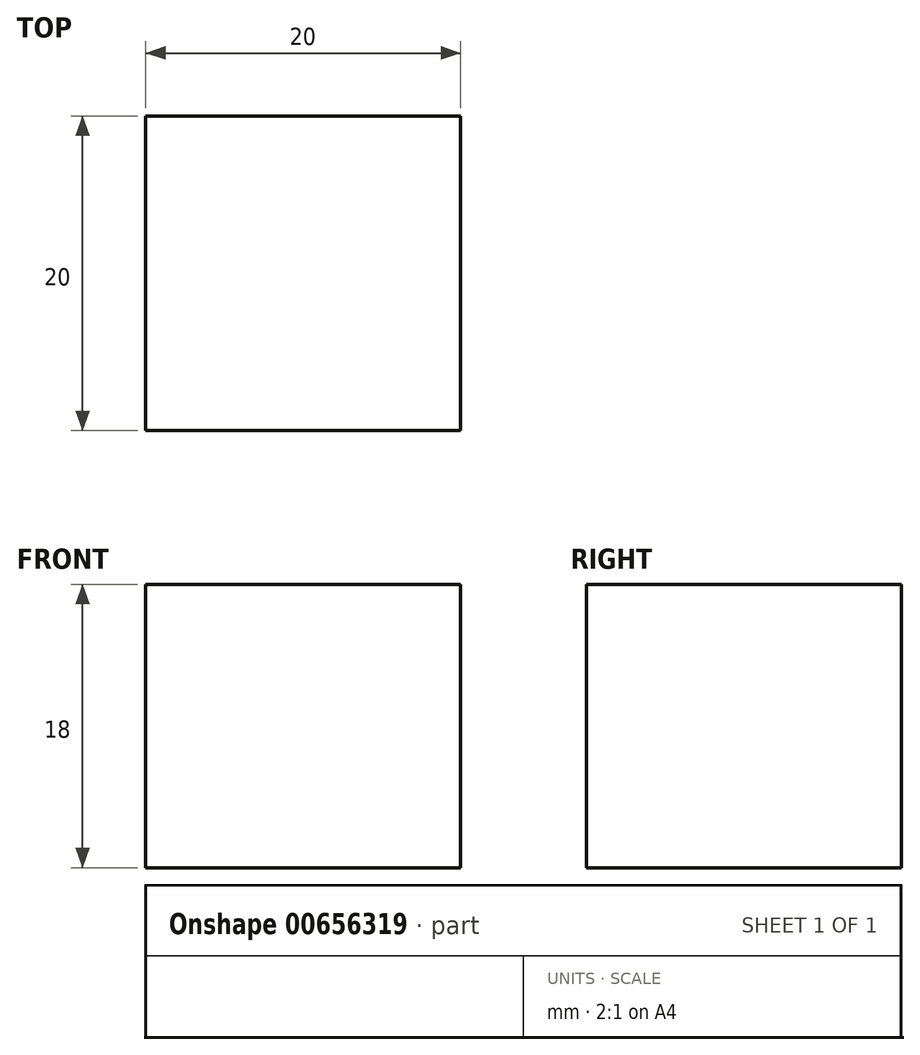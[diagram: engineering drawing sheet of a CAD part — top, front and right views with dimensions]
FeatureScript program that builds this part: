
annotation { "Feature Type Name" : "Feature", "Feature Type Description" : "" }
export const myFeature = defineFeature(function(context is Context, id is Id, definition is map)
    precondition{}
    {
        {
            var Q0;
            Q0=qCreatedBy(makeId("Front.planeOp"),FACE);
            var sketch = newSketch(context, id + "F0", { "sketchPlane" : qUnion([Q0])});
            skLineSegment(sketch, "E0.bottom", {"start": v(30.83, 38.52) * mm, "end": v(10.83, 38.52) * mm});
            skLineSegment(sketch, "E0.top", {"start": v(30.83, 20.52) * mm, "end": v(10.83, 20.52) * mm});
            skLineSegment(sketch, "E0.left", {"start": v(30.83, 38.52) * mm, "end": v(30.83, 20.52) * mm});
            skLineSegment(sketch, "E0.right", {"start": v(10.83, 38.52) * mm, "end": v(10.83, 20.52) * mm});
            skSolve(sketch);
        }
        {
            var Q0;
            Q0 = qSketchRegion(id + "F0", true);
            extrude(context, id + "F1", {"entities" : qUnion([Q0]), "depth" : 20 * mm, "offsetDistance" : 25 * mm});
        }
    });
